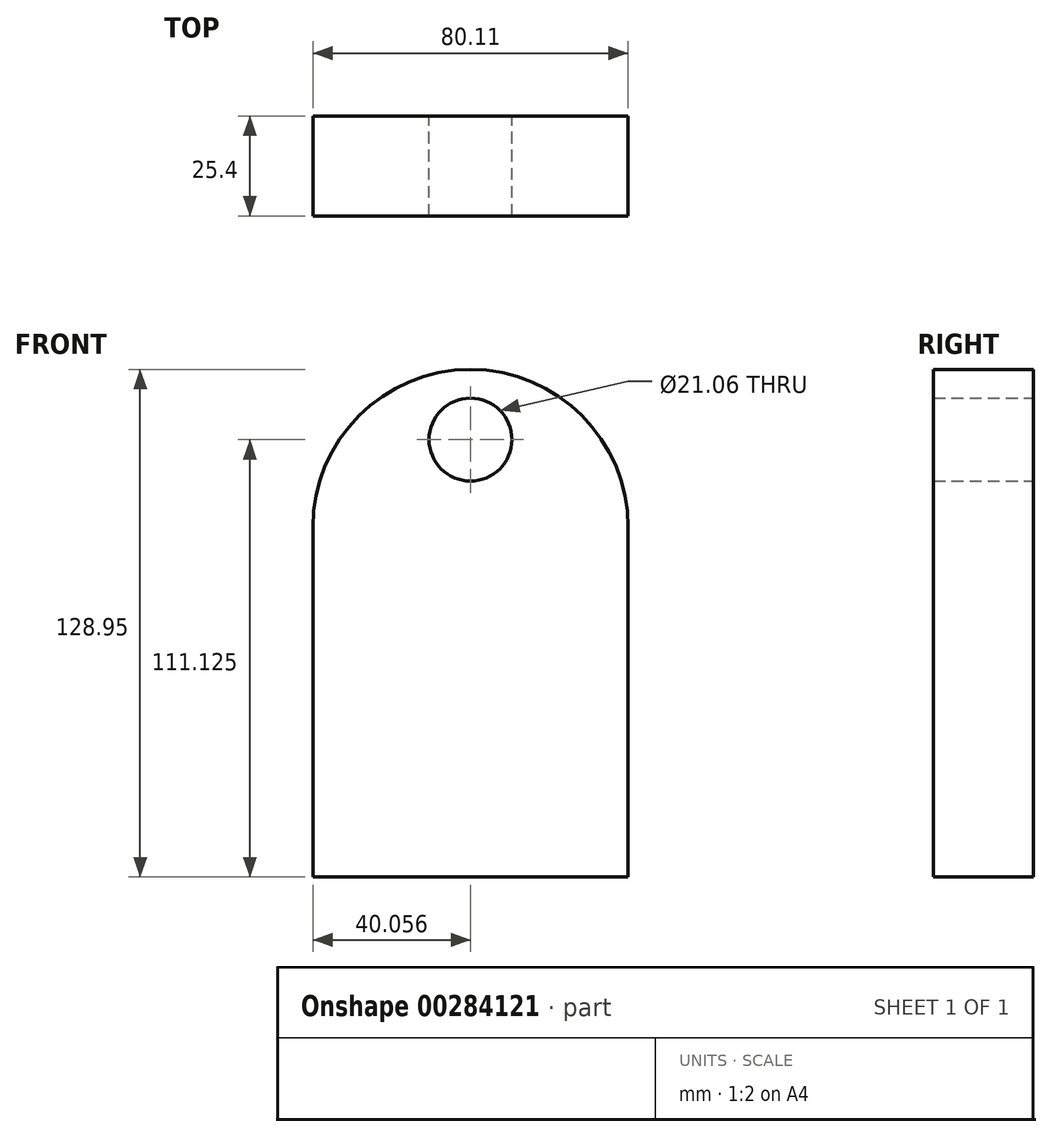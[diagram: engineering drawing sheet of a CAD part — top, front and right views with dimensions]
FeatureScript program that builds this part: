
annotation { "Feature Type Name" : "Feature", "Feature Type Description" : "" }
export const myFeature = defineFeature(function(context is Context, id is Id, definition is map)
    precondition{}
    {
        {
            var Q0;
            Q0=qCreatedBy(makeId("Front.planeOp"),FACE);
            var sketch = newSketch(context, id + "F0", { "sketchPlane" : qUnion([Q0])});
            skLineSegment(sketch, "E0.bottom", {"start": v(-32.47, 31.53) * mm, "end": v(47.64, 31.53) * mm});
            skLineSegment(sketch, "E0.top", {"start": v(-32.47, -57.37) * mm, "end": v(47.64, -57.37) * mm});
            skLineSegment(sketch, "E0.left", {"start": v(-32.47, 31.53) * mm, "end": v(-32.47, -57.37) * mm});
            skLineSegment(sketch, "E0.right", {"start": v(47.64, 31.53) * mm, "end": v(47.64, -57.37) * mm});
            skArc(sketch, "E1", {"start": v(47.64, 31.53) * mm, "mid": v(7.59, 71.58) * mm, "end": v(-32.47, 31.53) * mm});
            skCircle(sketch, "E2", {"center": v(7.59, 53.75) * mm, "radius": 10.53 * mm});
            skSolve(sketch);
        }
        {
            var Q0;
            Q0 = qSketchRegion(id + "F0", true);
            extrude(context, id + "F1", {"entities" : qUnion([Q0]), "depth" : 25.4 * mm});
        }
    });
